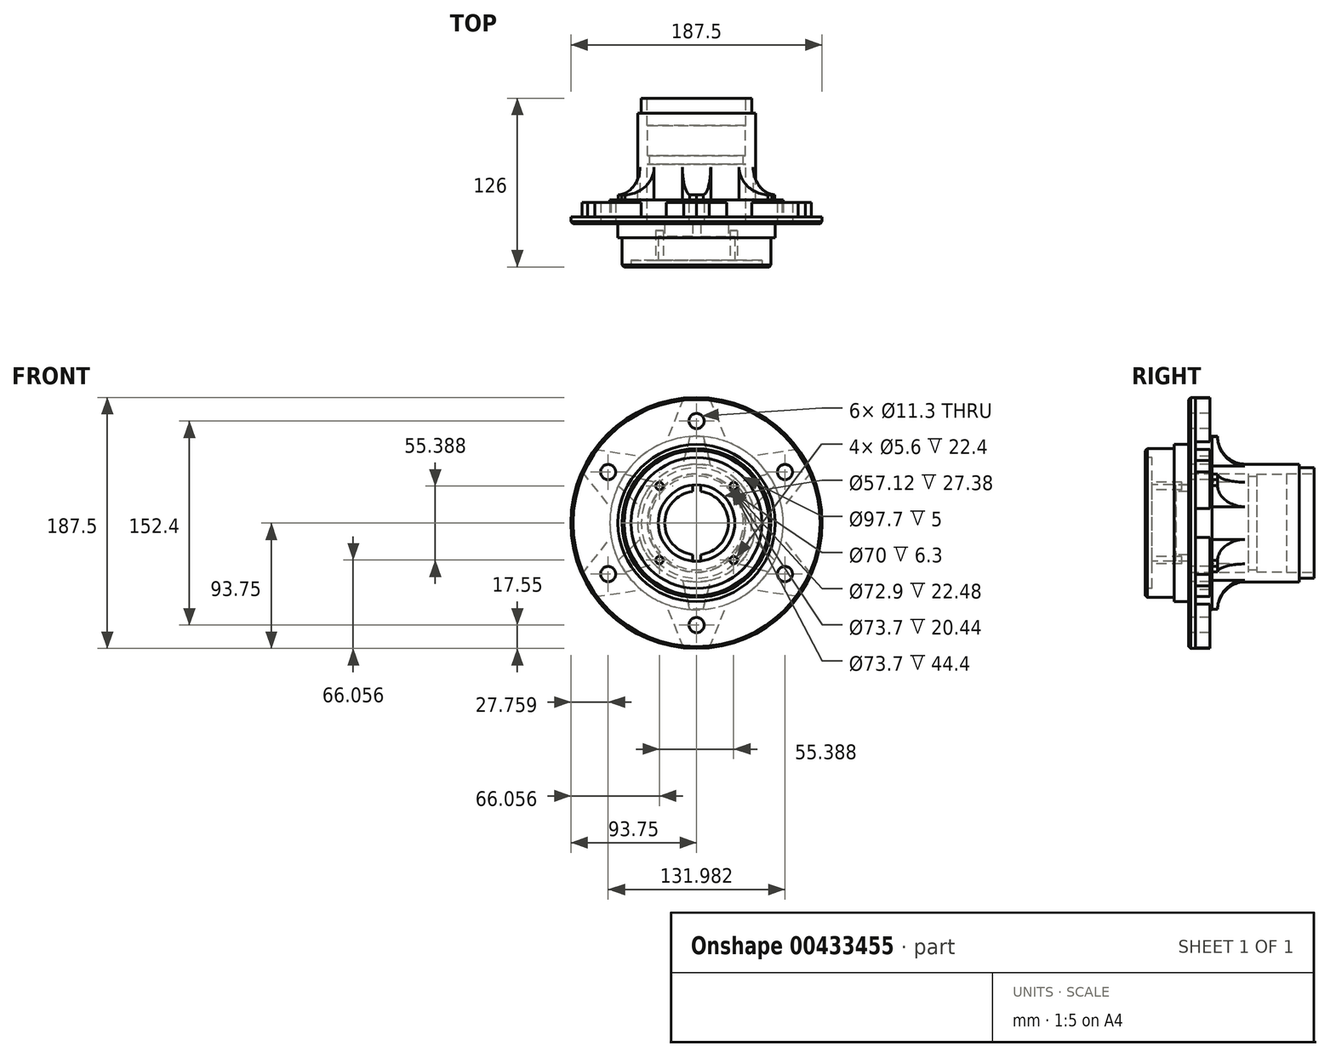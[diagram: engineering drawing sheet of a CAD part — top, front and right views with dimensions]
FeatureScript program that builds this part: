
annotation { "Feature Type Name" : "Feature", "Feature Type Description" : "" }
export const myFeature = defineFeature(function(context is Context, id is Id, definition is map)
    precondition{}
    {
        {
            var Q0;
            Q0=qCreatedBy(makeId("Front.planeOp"),FACE);
            var sketch = newSketch(context, id + "F0", { "sketchPlane" : qUnion([Q0])});
            skCircle(sketch, "E0", {"center": v(0, 0) * mm, "radius": 93.75 * mm});
            skSolve(sketch);
        }
        {
            var Q0;
            Q0=makeQuery(id+"F0.imprint","IMPRINT",FACE,{"disambiguationData":[TD([[makeQuery(id+"F0.imprint","IMPRINT",EDGE,{"derivedFrom":sQuery(id+"F0.wireOp",EDGE,"E0")}),1.0]])]});
            extrude(context, id + "F1", {"entities" : qUnion([Q0]), "endBound" : BoundingType.SYMMETRIC, "depth" : 5 * mm});
        }
        {
            var Q0;
            Q0=makeQuery(id+"F1.opExtrude","CAP_FACE",FACE,{"disambiguationData":[OSD([sQuery(id+"F0.wireOp",EDGE,"E0")])],"isStart":false});
            var sketch = newSketch(context, id + "F2", { "sketchPlane" : qUnion([Q0])});
            skCircle(sketch, "E1", {"center": v(0, 0) * mm, "radius": 58.67 * mm});
            skSolve(sketch);
        }
        {
            var Q0;
            Q0 = qSketchRegion(id + "F2", true);
            extrude(context, id + "F3", {"entities" : qUnion([Q0]), "operationType" : NewBodyOperationType.ADD, "depth" : 10.7 * mm});
        }
        {
            var Q0;
            Q0=makeQuery(id+"F3.opExtrude","CAP_FACE",FACE,{"disambiguationData":[OSD([sQuery(id+"F2.wireOp",EDGE,"E1")])],"isStart":false});
            var sketch = newSketch(context, id + "F4", { "sketchPlane" : qUnion([Q0])});
            skCircle(sketch, "E2", {"center": v(0, 0) * mm, "radius": 55.62 * mm});
            skSolve(sketch);
        }
        {
            var Q0;
            Q0 = qSketchRegion(id + "F4", true);
            extrude(context, id + "F5", {"entities" : qUnion([Q0]), "operationType" : NewBodyOperationType.ADD, "depth" : 21.7 * mm});
        }
        {
            var Q0;
            Q0=makeQuery(id+"F5.opExtrude","CAP_FACE",FACE,{"disambiguationData":[OSD([sQuery(id+"F4.wireOp",EDGE,"E2")])],"isStart":false});
            var sketch = newSketch(context, id + "F6", { "sketchPlane" : qUnion([Q0])});
            skCircle(sketch, "E3", {"center": v(0, 0) * mm, "radius": 48.85 * mm});
            skSolve(sketch);
        }
        {
            var Q0;
            Q0 = qSketchRegion(id + "F6", true);
            extrude(context, id + "F7", {"entities" : qUnion([Q0]), "operationType" : NewBodyOperationType.REMOVE, "oppositeDirection" : true, "depth" : 5 * mm});
        }
        {
            var Q0;
            Q0=makeQuery(id+"F7.boolean.opBoolean","COPY",FACE,{"derivedFrom":makeQuery(id+"F7.opExtrude","CAP_FACE",FACE,{"disambiguationData":[OSD([sQuery(id+"F6.wireOp",EDGE,"E3")])],"isStart":false})});
            var sketch = newSketch(context, id + "F8", { "sketchPlane" : qUnion([Q0])});
            skCircle(sketch, "E4", {"center": v(0, 0) * mm, "radius": 28.56 * mm});
            skSolve(sketch);
        }
        {
            var Q0;
            Q0=makeQuery(id+"F8.imprint","IMPRINT",FACE,{"disambiguationData":[TD([[makeQuery(id+"F8.imprint","IMPRINT",EDGE,{"derivedFrom":sQuery(id+"F8.wireOp",EDGE,"E4")}),1.0]])]});
            extrude(context, id + "F9", {"entities" : qUnion([Q0]), "operationType" : NewBodyOperationType.REMOVE, "oppositeDirection" : true, "depth" : 17.9 * mm});
        }
        {
            var Q0;
            Q0=makeQuery(id+"F9.boolean.opBoolean","COPY",FACE,{"derivedFrom":makeQuery(id+"F9.opExtrude","CAP_FACE",FACE,{"disambiguationData":[OSD([sQuery(id+"F8.wireOp",EDGE,"E4")])],"isStart":false})});
            var sketch = newSketch(context, id + "F10", { "sketchPlane" : qUnion([Q0])});
            skCircle(sketch, "E5", {"center": v(0, 0) * mm, "radius": 23.8 * mm});
            skSolve(sketch);
        }
        {
            var Q0;
            Q0 = qSketchRegion(id + "F10", true);
            extrude(context, id + "F11", {"entities" : qUnion([Q0]), "operationType" : NewBodyOperationType.REMOVE, "oppositeDirection" : true, "depth" : 9.3 * mm});
        }
        {
            var Q0;
            Q0=makeQuery(id+"F1.opExtrude","CAP_FACE",FACE,{"disambiguationData":[OSD([sQuery(id+"F0.wireOp",EDGE,"E0")])],"isStart":true});
            var sketch = newSketch(context, id + "F12", { "sketchPlane" : qUnion([Q0])});
            skLineSegment(sketch, "E6", {"start": v(0, -93.75) * mm, "end": v(9.62, -93.26) * mm});
            skLineSegment(sketch, "E7", {"start": v(9.62, -93.26) * mm, "end": v(22.62, -60.6) * mm});
            skLineSegment(sketch, "E8.MirrorCS", {"start": v(-9.62, -93.26) * mm, "end": v(-22.62, -60.6) * mm});
            skLineSegment(sketch, "E9", {"start": v(-9.62, -93.26) * mm, "end": v(0, -93.75) * mm});
            skLineSegment(sketch, "E10", {"start": v(22.62, -60.6) * mm, "end": v(-22.62, -60.6) * mm});
            skLineSegment(sketch, "E11.1.0", {"start": v(63.8, -10.71) * mm, "end": v(41.18, -49.89) * mm});
            skLineSegment(sketch, "E11.1.1", {"start": v(85.57, -38.3) * mm, "end": v(63.8, -10.71) * mm});
            skLineSegment(sketch, "E11.1.2", {"start": v(75.95, -54.96) * mm, "end": v(81.19, -46.88) * mm});
            skLineSegment(sketch, "E11.1.3", {"start": v(81.19, -46.88) * mm, "end": v(85.57, -38.3) * mm});
            skLineSegment(sketch, "E11.1.4", {"start": v(75.95, -54.96) * mm, "end": v(41.18, -49.89) * mm});
            skLineSegment(sketch, "E11.2.0", {"start": v(41.18, 49.89) * mm, "end": v(63.8, 10.71) * mm});
            skLineSegment(sketch, "E11.2.1", {"start": v(75.95, 54.96) * mm, "end": v(41.18, 49.89) * mm});
            skLineSegment(sketch, "E11.2.2", {"start": v(85.57, 38.3) * mm, "end": v(81.19, 46.87) * mm});
            skLineSegment(sketch, "E11.2.3", {"start": v(81.19, 46.87) * mm, "end": v(75.95, 54.96) * mm});
            skLineSegment(sketch, "E11.2.4", {"start": v(85.57, 38.3) * mm, "end": v(63.8, 10.71) * mm});
            skLineSegment(sketch, "E11.3.0", {"start": v(-22.62, 60.6) * mm, "end": v(22.62, 60.6) * mm});
            skLineSegment(sketch, "E11.3.1", {"start": v(-9.62, 93.26) * mm, "end": v(-22.62, 60.6) * mm});
            skLineSegment(sketch, "E11.3.2", {"start": v(9.62, 93.26) * mm, "end": v(0, 93.75) * mm});
            skLineSegment(sketch, "E11.3.3", {"start": v(0, 93.75) * mm, "end": v(-9.62, 93.26) * mm});
            skLineSegment(sketch, "E11.3.4", {"start": v(9.62, 93.26) * mm, "end": v(22.62, 60.6) * mm});
            skLineSegment(sketch, "E11.4.0", {"start": v(-63.8, 10.71) * mm, "end": v(-41.18, 49.89) * mm});
            skLineSegment(sketch, "E11.4.1", {"start": v(-85.57, 38.3) * mm, "end": v(-63.8, 10.71) * mm});
            skLineSegment(sketch, "E11.4.2", {"start": v(-75.95, 54.96) * mm, "end": v(-81.19, 46.88) * mm});
            skLineSegment(sketch, "E11.4.3", {"start": v(-81.19, 46.88) * mm, "end": v(-85.57, 38.3) * mm});
            skLineSegment(sketch, "E11.4.4", {"start": v(-75.95, 54.96) * mm, "end": v(-41.18, 49.89) * mm});
            skLineSegment(sketch, "E11.5.0", {"start": v(-41.18, -49.89) * mm, "end": v(-63.8, -10.71) * mm});
            skLineSegment(sketch, "E11.5.1", {"start": v(-75.95, -54.96) * mm, "end": v(-41.18, -49.89) * mm});
            skLineSegment(sketch, "E11.5.2", {"start": v(-85.57, -38.3) * mm, "end": v(-81.19, -46.88) * mm});
            skLineSegment(sketch, "E11.5.3", {"start": v(-81.19, -46.88) * mm, "end": v(-75.95, -54.96) * mm});
            skLineSegment(sketch, "E11.5.4", {"start": v(-85.57, -38.3) * mm, "end": v(-63.8, -10.71) * mm});
            skPoint(sketch, "E11.center", {"position": v(0, 0) * mm});
            skSolve(sketch);
        }
        {
            var Q0;
            Q0 = qSketchRegion(id + "F12", true);
            extrude(context, id + "F13", {"entities" : qUnion([Q0]), "operationType" : NewBodyOperationType.ADD, "depth" : 10.8 * mm});
        }
        {
            var Q0;
            {var subQ0=sQuery(id+"F0.wireOp",EDGE,"E0");var subQ1=makeQuery(id+"F1.opExtrude","CAP_FACE",FACE,{"disambiguationData":[OSD([subQ0])],"isStart":true});Q0=makeQuery(id+"F13.boolean.opBoolean","SPLIT",FACE,{"disambiguationData":[TD([makeQuery(id+"F1.opExtrude","SWEPT_FACE",FACE,{"disambiguationData":[OSD([subQ0])]}),subQ1,makeQuery(id+"F13.opExtrude","SWEPT_FACE",FACE,{"disambiguationData":[OSD([sQuery(id+"F12.wireOp",EDGE,"E6")])]}),makeQuery(id+"F13.opExtrude","SWEPT_FACE",FACE,{"disambiguationData":[OSD([sQuery(id+"F12.wireOp",EDGE,"E7")])]}),makeQuery(id+"F13.opExtrude","SWEPT_FACE",FACE,{"disambiguationData":[OSD([sQuery(id+"F12.wireOp",EDGE,"E8.MirrorCS")])]}),makeQuery(id+"F13.opExtrude","SWEPT_FACE",FACE,{"disambiguationData":[OSD([sQuery(id+"F12.wireOp",EDGE,"E9")])]}),makeQuery(id+"F13.opExtrude","SWEPT_FACE",FACE,{"disambiguationData":[OSD([sQuery(id+"F12.wireOp",EDGE,"E10")])]}),makeQuery(id+"F13.opExtrude","SWEPT_FACE",FACE,{"disambiguationData":[OSD([sQuery(id+"F12.wireOp",EDGE,"E11.1.0")])]}),makeQuery(id+"F13.opExtrude","SWEPT_FACE",FACE,{"disambiguationData":[OSD([sQuery(id+"F12.wireOp",EDGE,"E11.1.1")])]}),makeQuery(id+"F13.opExtrude","SWEPT_FACE",FACE,{"disambiguationData":[OSD([sQuery(id+"F12.wireOp",EDGE,"E11.1.2")])]}),makeQuery(id+"F13.opExtrude","SWEPT_FACE",FACE,{"disambiguationData":[OSD([sQuery(id+"F12.wireOp",EDGE,"E11.1.3")])]}),makeQuery(id+"F13.opExtrude","SWEPT_FACE",FACE,{"disambiguationData":[OSD([sQuery(id+"F12.wireOp",EDGE,"E11.1.4")])]}),makeQuery(id+"F13.opExtrude","SWEPT_FACE",FACE,{"disambiguationData":[OSD([sQuery(id+"F12.wireOp",EDGE,"E11.2.0")])]}),makeQuery(id+"F13.opExtrude","SWEPT_FACE",FACE,{"disambiguationData":[OSD([sQuery(id+"F12.wireOp",EDGE,"E11.2.1")])]}),makeQuery(id+"F13.opExtrude","SWEPT_FACE",FACE,{"disambiguationData":[OSD([sQuery(id+"F12.wireOp",EDGE,"E11.2.2")])]}),makeQuery(id+"F13.opExtrude","SWEPT_FACE",FACE,{"disambiguationData":[OSD([sQuery(id+"F12.wireOp",EDGE,"E11.2.3")])]}),makeQuery(id+"F13.opExtrude","SWEPT_FACE",FACE,{"disambiguationData":[OSD([sQuery(id+"F12.wireOp",EDGE,"E11.2.4")])]}),makeQuery(id+"F13.opExtrude","SWEPT_FACE",FACE,{"disambiguationData":[OSD([sQuery(id+"F12.wireOp",EDGE,"E11.3.0")])]}),makeQuery(id+"F13.opExtrude","SWEPT_FACE",FACE,{"disambiguationData":[OSD([sQuery(id+"F12.wireOp",EDGE,"E11.3.1")])]}),makeQuery(id+"F13.opExtrude","SWEPT_FACE",FACE,{"disambiguationData":[OSD([sQuery(id+"F12.wireOp",EDGE,"E11.3.2")])]}),makeQuery(id+"F13.opExtrude","SWEPT_FACE",FACE,{"disambiguationData":[OSD([sQuery(id+"F12.wireOp",EDGE,"E11.3.3")])]}),makeQuery(id+"F13.opExtrude","SWEPT_FACE",FACE,{"disambiguationData":[OSD([sQuery(id+"F12.wireOp",EDGE,"E11.3.4")])]}),makeQuery(id+"F13.opExtrude","SWEPT_FACE",FACE,{"disambiguationData":[OSD([sQuery(id+"F12.wireOp",EDGE,"E11.4.0")])]}),makeQuery(id+"F13.opExtrude","SWEPT_FACE",FACE,{"disambiguationData":[OSD([sQuery(id+"F12.wireOp",EDGE,"E11.4.1")])]}),makeQuery(id+"F13.opExtrude","SWEPT_FACE",FACE,{"disambiguationData":[OSD([sQuery(id+"F12.wireOp",EDGE,"E11.4.2")])]}),makeQuery(id+"F13.opExtrude","SWEPT_FACE",FACE,{"disambiguationData":[OSD([sQuery(id+"F12.wireOp",EDGE,"E11.4.3")])]}),makeQuery(id+"F13.opExtrude","SWEPT_FACE",FACE,{"disambiguationData":[OSD([sQuery(id+"F12.wireOp",EDGE,"E11.4.4")])]}),makeQuery(id+"F13.opExtrude","SWEPT_FACE",FACE,{"disambiguationData":[OSD([sQuery(id+"F12.wireOp",EDGE,"E11.5.0")])]}),makeQuery(id+"F13.opExtrude","SWEPT_FACE",FACE,{"disambiguationData":[OSD([sQuery(id+"F12.wireOp",EDGE,"E11.5.1")])]}),makeQuery(id+"F13.opExtrude","SWEPT_FACE",FACE,{"disambiguationData":[OSD([sQuery(id+"F12.wireOp",EDGE,"E11.5.2")])]}),makeQuery(id+"F13.opExtrude","SWEPT_FACE",FACE,{"disambiguationData":[OSD([sQuery(id+"F12.wireOp",EDGE,"E11.5.3")])]}),makeQuery(id+"F13.opExtrude","SWEPT_FACE",FACE,{"disambiguationData":[OSD([sQuery(id+"F12.wireOp",EDGE,"E11.5.4")])]})])],"derivedFrom":subQ1});}
            var sketch = newSketch(context, id + "F14", { "sketchPlane" : qUnion([Q0])});
            skCircle(sketch, "E12", {"center": v(0, 0) * mm, "radius": 64.7 * mm});
            skSolve(sketch);
        }
        {
            var Q0;
            Q0 = qSketchRegion(id + "F14", true);
            extrude(context, id + "F15", {"entities" : qUnion([Q0]), "operationType" : NewBodyOperationType.ADD, "depth" : 88.6 * mm});
        }
        {
            var Q0;
            Q0=makeQuery(id+"F15.opExtrude","CAP_FACE",FACE,{"disambiguationData":[OSD([sQuery(id+"F14.wireOp",EDGE,"E12")])],"isStart":false});
            var sketch = newSketch(context, id + "F16", { "sketchPlane" : qUnion([Q0])});
            skCircle(sketch, "E13", {"center": v(0, 0) * mm, "radius": 44 * mm});
            skSolve(sketch);
        }
        {
            var Q0;
            Q0=makeQuery(id+"F16.imprint","IMPRINT",FACE,{"disambiguationData":[TD([[makeQuery(id+"F16.imprint","IMPRINT",EDGE,{"derivedFrom":sQuery(id+"F16.wireOp",EDGE,"E13")}),-1.0]])]});
            extrude(context, id + "F17", {"entities" : qUnion([Q0]), "operationType" : NewBodyOperationType.REMOVE, "oppositeDirection" : true, "depth" : 76 * mm});
        }
        {
            var Q0;
            Q0=makeQuery(id+"F17.boolean.opBoolean","COPY",FACE,{"derivedFrom":makeQuery(id+"F17.opExtrude","CAP_FACE",FACE,{"disambiguationData":[OSD([sQuery(id+"F14.wireOp",EDGE,"E12"),sQuery(id+"F16.wireOp",EDGE,"E13")])],"isStart":false})});
            var sketch = newSketch(context, id + "F18", { "sketchPlane" : qUnion([Q0])});
            skLineSegment(sketch, "E14", {"start": v(-5, -64.5) * mm, "end": v(-10.58, -42.7) * mm});
            skLineSegment(sketch, "E15", {"start": v(-10.58, -42.7) * mm, "end": v(0, -44) * mm});
            skLineSegment(sketch, "E16.MirrorCS", {"start": v(5, -64.5) * mm, "end": v(10.58, -42.7) * mm});
            skLineSegment(sketch, "E17.MirrorCS", {"start": v(10.58, -42.7) * mm, "end": v(0, -44) * mm});
            skLineSegment(sketch, "E18.1.0", {"start": v(53.37, -36.58) * mm, "end": v(31.7, -30.52) * mm});
            skLineSegment(sketch, "E18.1.1", {"start": v(56.03, -32.35) * mm, "end": v(53.37, -36.58) * mm});
            skLineSegment(sketch, "E18.1.2", {"start": v(56.03, -32.35) * mm, "end": v(58.36, -27.93) * mm});
            skLineSegment(sketch, "E18.1.3", {"start": v(58.36, -27.93) * mm, "end": v(42.28, -12.2) * mm});
            skLineSegment(sketch, "E18.1.4", {"start": v(42.28, -12.2) * mm, "end": v(38.1, -22) * mm});
            skLineSegment(sketch, "E18.1.5", {"start": v(31.7, -30.52) * mm, "end": v(38.1, -22) * mm});
            skLineSegment(sketch, "E18.2.0", {"start": v(58.36, 27.93) * mm, "end": v(42.28, 12.2) * mm});
            skLineSegment(sketch, "E18.2.1", {"start": v(56.03, 32.35) * mm, "end": v(58.36, 27.93) * mm});
            skLineSegment(sketch, "E18.2.2", {"start": v(56.03, 32.35) * mm, "end": v(53.37, 36.58) * mm});
            skLineSegment(sketch, "E18.2.3", {"start": v(53.37, 36.58) * mm, "end": v(31.7, 30.52) * mm});
            skLineSegment(sketch, "E18.2.4", {"start": v(31.7, 30.52) * mm, "end": v(38.1, 22) * mm});
            skLineSegment(sketch, "E18.2.5", {"start": v(42.28, 12.2) * mm, "end": v(38.1, 22) * mm});
            skLineSegment(sketch, "E18.3.0", {"start": v(5, 64.5) * mm, "end": v(10.58, 42.7) * mm});
            skLineSegment(sketch, "E18.3.1", {"start": v(0, 64.7) * mm, "end": v(5, 64.5) * mm});
            skLineSegment(sketch, "E18.3.2", {"start": v(0, 64.7) * mm, "end": v(-5, 64.5) * mm});
            skLineSegment(sketch, "E18.3.3", {"start": v(-5, 64.5) * mm, "end": v(-10.58, 42.7) * mm});
            skLineSegment(sketch, "E18.3.4", {"start": v(-10.58, 42.7) * mm, "end": v(0, 44) * mm});
            skLineSegment(sketch, "E18.3.5", {"start": v(10.58, 42.7) * mm, "end": v(0, 44) * mm});
            skLineSegment(sketch, "E18.4.0", {"start": v(-53.37, 36.58) * mm, "end": v(-31.7, 30.52) * mm});
            skLineSegment(sketch, "E18.4.1", {"start": v(-56.03, 32.35) * mm, "end": v(-53.37, 36.58) * mm});
            skLineSegment(sketch, "E18.4.2", {"start": v(-56.03, 32.35) * mm, "end": v(-58.36, 27.93) * mm});
            skLineSegment(sketch, "E18.4.3", {"start": v(-58.36, 27.93) * mm, "end": v(-42.28, 12.2) * mm});
            skLineSegment(sketch, "E18.4.4", {"start": v(-42.28, 12.2) * mm, "end": v(-38.1, 22) * mm});
            skLineSegment(sketch, "E18.4.5", {"start": v(-31.7, 30.52) * mm, "end": v(-38.1, 22) * mm});
            skLineSegment(sketch, "E18.5.0", {"start": v(-58.36, -27.93) * mm, "end": v(-42.28, -12.2) * mm});
            skLineSegment(sketch, "E18.5.1", {"start": v(-56.03, -32.35) * mm, "end": v(-58.36, -27.93) * mm});
            skLineSegment(sketch, "E18.5.2", {"start": v(-56.03, -32.35) * mm, "end": v(-53.37, -36.58) * mm});
            skLineSegment(sketch, "E18.5.3", {"start": v(-53.37, -36.58) * mm, "end": v(-31.7, -30.52) * mm});
            skLineSegment(sketch, "E18.5.4", {"start": v(-31.7, -30.52) * mm, "end": v(-38.1, -22) * mm});
            skLineSegment(sketch, "E18.5.5", {"start": v(-42.28, -12.2) * mm, "end": v(-38.1, -22) * mm});
            skPoint(sketch, "E18.center", {"position": v(0, 0) * mm});
            skLineSegment(sketch, "E19", {"start": v(-5, -64.5) * mm, "end": v(5, -64.5) * mm});
            skSolve(sketch);
        }
        {
            var Q0;
            Q0 = qSketchRegion(id + "F18", true);
            extrude(context, id + "F19", {"entities" : qUnion([Q0]), "depth" : 4 * mm});
        }
        {
            var Q0;
            Q0=makeQuery(id+"F1.opExtrude","SWEPT_BODY",BODY,{"disambiguationData":[OSD([sQuery(id+"F0.wireOp",EDGE,"E0")])]});
            var Q1;
            Q1=makeQuery(id+"F19.opExtrude","SWEPT_BODY",BODY,{"disambiguationData":[OSD([sQuery(id+"F18.wireOp",EDGE,"E18.3.0"),sQuery(id+"F18.wireOp",EDGE,"E18.3.1"),sQuery(id+"F18.wireOp",EDGE,"E18.3.2"),sQuery(id+"F18.wireOp",EDGE,"E18.3.3"),sQuery(id+"F18.wireOp",EDGE,"E18.3.4"),sQuery(id+"F18.wireOp",EDGE,"E18.3.5")])]});
            var Q2;
            Q2=makeQuery(id+"F19.opExtrude","SWEPT_BODY",BODY,{"disambiguationData":[OSD([sQuery(id+"F18.wireOp",EDGE,"E18.2.0"),sQuery(id+"F18.wireOp",EDGE,"E18.2.1"),sQuery(id+"F18.wireOp",EDGE,"E18.2.2"),sQuery(id+"F18.wireOp",EDGE,"E18.2.3"),sQuery(id+"F18.wireOp",EDGE,"E18.2.4"),sQuery(id+"F18.wireOp",EDGE,"E18.2.5")])]});
            var Q3;
            Q3=makeQuery(id+"F19.opExtrude","SWEPT_BODY",BODY,{"disambiguationData":[OSD([sQuery(id+"F18.wireOp",EDGE,"E18.1.0"),sQuery(id+"F18.wireOp",EDGE,"E18.1.1"),sQuery(id+"F18.wireOp",EDGE,"E18.1.2"),sQuery(id+"F18.wireOp",EDGE,"E18.1.3"),sQuery(id+"F18.wireOp",EDGE,"E18.1.4"),sQuery(id+"F18.wireOp",EDGE,"E18.1.5")])]});
            var Q4;
            Q4=makeQuery(id+"F19.opExtrude","SWEPT_BODY",BODY,{"disambiguationData":[OSD([sQuery(id+"F18.wireOp",EDGE,"E14"),sQuery(id+"F18.wireOp",EDGE,"E15"),sQuery(id+"F18.wireOp",EDGE,"E16.MirrorCS"),sQuery(id+"F18.wireOp",EDGE,"E17.MirrorCS"),sQuery(id+"F18.wireOp",EDGE,"E19")])]});
            var Q5;
            Q5=makeQuery(id+"F19.opExtrude","SWEPT_BODY",BODY,{"disambiguationData":[OSD([sQuery(id+"F18.wireOp",EDGE,"E18.5.0"),sQuery(id+"F18.wireOp",EDGE,"E18.5.1"),sQuery(id+"F18.wireOp",EDGE,"E18.5.2"),sQuery(id+"F18.wireOp",EDGE,"E18.5.3"),sQuery(id+"F18.wireOp",EDGE,"E18.5.4"),sQuery(id+"F18.wireOp",EDGE,"E18.5.5")])]});
            var Q6;
            Q6=makeQuery(id+"F19.opExtrude","SWEPT_BODY",BODY,{"disambiguationData":[OSD([sQuery(id+"F18.wireOp",EDGE,"E18.4.0"),sQuery(id+"F18.wireOp",EDGE,"E18.4.1"),sQuery(id+"F18.wireOp",EDGE,"E18.4.2"),sQuery(id+"F18.wireOp",EDGE,"E18.4.3"),sQuery(id+"F18.wireOp",EDGE,"E18.4.4"),sQuery(id+"F18.wireOp",EDGE,"E18.4.5")])]});
            booleanBodies(context, id + "F20", {"operationType" : BooleanOperationType.UNION, "tools" : qUnion([Q0, Q1, Q2, Q3, Q4, Q5, Q6])});
        }
        {
            var Q0;
            Q0=makeQuery(id+"F15.opExtrude","CAP_FACE",FACE,{"disambiguationData":[OSD([sQuery(id+"F14.wireOp",EDGE,"E12")])],"isStart":false});
            var sketch = newSketch(context, id + "F21", { "sketchPlane" : qUnion([Q0])});
            skCircle(sketch, "E20", {"center": v(0, 0) * mm, "radius": 36.85 * mm});
            skSolve(sketch);
        }
        {
            var Q0;
            Q0 = qSketchRegion(id + "F21", true);
            extrude(context, id + "F22", {"entities" : qUnion([Q0]), "operationType" : NewBodyOperationType.REMOVE, "oppositeDirection" : true, "depth" : 20.44 * mm});
        }
        {
            var Q0;
            Q0=makeQuery(id+"F22.boolean.opBoolean","COPY",FACE,{"derivedFrom":makeQuery(id+"F22.opExtrude","CAP_FACE",FACE,{"disambiguationData":[OSD([sQuery(id+"F21.wireOp",EDGE,"E20")])],"isStart":false})});
            var sketch = newSketch(context, id + "F23", { "sketchPlane" : qUnion([Q0])});
            skCircle(sketch, "E21", {"center": v(0, 0) * mm, "radius": 36.45 * mm});
            skSolve(sketch);
        }
        {
            var Q0;
            Q0 = qSketchRegion(id + "F23", true);
            extrude(context, id + "F24", {"entities" : qUnion([Q0]), "operationType" : NewBodyOperationType.REMOVE, "oppositeDirection" : true, "depth" : 22.48 * mm});
        }
        {
            var Q0;
            Q0=makeQuery(id+"F24.boolean.opBoolean","COPY",FACE,{"derivedFrom":makeQuery(id+"F24.opExtrude","CAP_FACE",FACE,{"disambiguationData":[OSD([sQuery(id+"F23.wireOp",EDGE,"E21")])],"isStart":false})});
            var sketch = newSketch(context, id + "F25", { "sketchPlane" : qUnion([Q0])});
            skCircle(sketch, "E22", {"center": v(0, 0) * mm, "radius": 35 * mm});
            skSolve(sketch);
        }
        {
            var Q0;
            Q0 = qSketchRegion(id + "F25", true);
            extrude(context, id + "F26", {"entities" : qUnion([Q0]), "operationType" : NewBodyOperationType.REMOVE, "oppositeDirection" : true, "depth" : 6.3 * mm});
        }
        {
            var Q0;
            Q0=makeQuery(id+"F15.opExtrude","CAP_FACE",FACE,{"disambiguationData":[OSD([sQuery(id+"F14.wireOp",EDGE,"E12")])],"isStart":false});
            var sketch = newSketch(context, id + "F27", { "sketchPlane" : qUnion([Q0])});
            skCircle(sketch, "E23", {"center": v(0, 0) * mm, "radius": 41.25 * mm});
            skSolve(sketch);
        }
        {
            var Q0;
            Q0=makeQuery(id+"F11.boolean.opBoolean","COPY",FACE,{"derivedFrom":makeQuery(id+"F11.opExtrude","CAP_FACE",FACE,{"disambiguationData":[OSD([sQuery(id+"F10.wireOp",EDGE,"E5")])],"isStart":false})});
            extrude(context, id + "F28", {"entities" : qUnion([Q0]), "operationType" : NewBodyOperationType.REMOVE, "oppositeDirection" : true, "depth" : 44.4 * mm});
        }
        {
            var Q0;
            Q0=makeQuery(id+"F9.boolean.opBoolean","COPY",FACE,{"derivedFrom":makeQuery(id+"F9.opExtrude","CAP_FACE",FACE,{"disambiguationData":[OSD([sQuery(id+"F8.wireOp",EDGE,"E4")])],"isStart":false})});
            var sketch = newSketch(context, id + "F29", { "sketchPlane" : qUnion([Q0])});
            skArc(sketch, "E24", {"start": v(3, 29.2) * mm, "mid": v(0, 29.35) * mm, "end": v(-3, 29.2) * mm});
            skLineSegment(sketch, "E25.0", {"start": v(3, 23.8) * mm, "end": v(3, 28.56) * mm});
            skLineSegment(sketch, "E26.0", {"start": v(-3, 23.8) * mm, "end": v(-3, 28.56) * mm});
            skLineSegment(sketch, "E27", {"start": v(-3, 28.56) * mm, "end": v(-3, 29.2) * mm});
            skLineSegment(sketch, "E28", {"start": v(3, 28.56) * mm, "end": v(3, 29.2) * mm});
            skLineSegment(sketch, "E29", {"start": v(-3, 23.8) * mm, "end": v(-3, 23.67) * mm});
            skLineSegment(sketch, "E30", {"start": v(3, 23.8) * mm, "end": v(3, 23.67) * mm});
            skLineSegment(sketch, "E31.MirrorCS", {"start": v(-3, -23.8) * mm, "end": v(-3, -23.67) * mm});
            skLineSegment(sketch, "E32.MirrorCS", {"start": v(3, -23.8) * mm, "end": v(3, -23.67) * mm});
            skLineSegment(sketch, "E33.MirrorCS", {"start": v(3, -28.56) * mm, "end": v(3, -29.2) * mm});
            skLineSegment(sketch, "E34.MirrorCS", {"start": v(-3, -28.56) * mm, "end": v(-3, -29.2) * mm});
            skLineSegment(sketch, "E35.MirrorCS", {"start": v(3, -23.8) * mm, "end": v(3, -28.56) * mm});
            skLineSegment(sketch, "E36.MirrorCS", {"start": v(-3, -23.8) * mm, "end": v(-3, -28.56) * mm});
            skArc(sketch, "E37.MirrorCS", {"start": v(3, -29.2) * mm, "mid": v(0, -29.35) * mm, "end": v(-3, -29.2) * mm});
            skArc(sketch, "E38", {"start": v(-3, -23.37) * mm, "mid": v(0, -23.56) * mm, "end": v(3, -23.37) * mm});
            skLineSegment(sketch, "E39", {"start": v(-3, 23.67) * mm, "end": v(-3, 23.37) * mm});
            skLineSegment(sketch, "E40", {"start": v(3, 23.67) * mm, "end": v(3, 23.37) * mm});
            skLineSegment(sketch, "E41", {"start": v(-3, -23.67) * mm, "end": v(-3, -23.37) * mm});
            skLineSegment(sketch, "E42", {"start": v(3, -23.67) * mm, "end": v(3, -23.37) * mm});
            skArc(sketch, "E43.trimOffspring", {"start": v(3, 23.37) * mm, "mid": v(0, 23.56) * mm, "end": v(-3, 23.37) * mm});
            skSolve(sketch);
        }
        {
            var Q0;
            Q0=makeQuery(id+"F27.imprint","IMPRINT",FACE,{"disambiguationData":[TD([[makeQuery(id+"F27.imprint","IMPRINT",EDGE,{"derivedFrom":makeQuery(id+"F22.boolean.opBoolean","COPY",EDGE,{"derivedFrom":makeQuery(id+"F22.opExtrude","CAP_EDGE",EDGE,{"disambiguationData":[OSD([sQuery(id+"F21.wireOp",EDGE,"E20")])],"isStart":true})})}),1.0]])]});
            var Q1;
            Q1=makeQuery(id+"F27.imprint","IMPRINT",FACE,{"disambiguationData":[TD([[makeQuery(id+"F27.imprint","IMPRINT",EDGE,{"derivedFrom":sQuery(id+"F27.wireOp",EDGE,"E23")}),-1.0]])]});
            extrude(context, id + "F30", {"entities" : qUnion([Q0, Q1]), "operationType" : NewBodyOperationType.REMOVE, "oppositeDirection" : true, "depth" : 11.1 * mm});
        }
        {
            var Q0;
            Q0=makeQuery(id+"F20.opBoolean","INTERSECT",EDGE,{"derivedFrom":[makeQuery(id+"F17.boolean.opBoolean","COPY",FACE,{"derivedFrom":makeQuery(id+"F17.opExtrude","SWEPT_FACE",FACE,{"disambiguationData":[OSD([sQuery(id+"F16.wireOp",EDGE,"E13")])]})}),makeQuery(id+"F19.opExtrude","CAP_FACE",FACE,{"disambiguationData":[OSD([sQuery(id+"F18.wireOp",EDGE,"E14"),sQuery(id+"F18.wireOp",EDGE,"E15"),sQuery(id+"F18.wireOp",EDGE,"E16.MirrorCS"),sQuery(id+"F18.wireOp",EDGE,"E17.MirrorCS"),sQuery(id+"F18.wireOp",EDGE,"E19")])],"isStart":false})]});
            var Q1;
            Q1=makeQuery(id+"F20.opBoolean","INTERSECT",EDGE,{"derivedFrom":[makeQuery(id+"F17.boolean.opBoolean","COPY",FACE,{"derivedFrom":makeQuery(id+"F17.opExtrude","SWEPT_FACE",FACE,{"disambiguationData":[OSD([sQuery(id+"F16.wireOp",EDGE,"E13")])]})}),makeQuery(id+"F19.opExtrude","CAP_FACE",FACE,{"disambiguationData":[OSD([sQuery(id+"F18.wireOp",EDGE,"E18.5.0"),sQuery(id+"F18.wireOp",EDGE,"E18.5.1"),sQuery(id+"F18.wireOp",EDGE,"E18.5.2"),sQuery(id+"F18.wireOp",EDGE,"E18.5.3"),sQuery(id+"F18.wireOp",EDGE,"E18.5.4"),sQuery(id+"F18.wireOp",EDGE,"E18.5.5")])],"isStart":false})]});
            var Q2;
            Q2=makeQuery(id+"F20.opBoolean","INTERSECT",EDGE,{"derivedFrom":[makeQuery(id+"F17.boolean.opBoolean","COPY",FACE,{"derivedFrom":makeQuery(id+"F17.opExtrude","SWEPT_FACE",FACE,{"disambiguationData":[OSD([sQuery(id+"F16.wireOp",EDGE,"E13")])]})}),makeQuery(id+"F19.opExtrude","CAP_FACE",FACE,{"disambiguationData":[OSD([sQuery(id+"F18.wireOp",EDGE,"E18.1.0"),sQuery(id+"F18.wireOp",EDGE,"E18.1.1"),sQuery(id+"F18.wireOp",EDGE,"E18.1.2"),sQuery(id+"F18.wireOp",EDGE,"E18.1.3"),sQuery(id+"F18.wireOp",EDGE,"E18.1.4"),sQuery(id+"F18.wireOp",EDGE,"E18.1.5")])],"isStart":false})]});
            var Q3;
            Q3=makeQuery(id+"F20.opBoolean","INTERSECT",EDGE,{"derivedFrom":[makeQuery(id+"F17.boolean.opBoolean","COPY",FACE,{"derivedFrom":makeQuery(id+"F17.opExtrude","SWEPT_FACE",FACE,{"disambiguationData":[OSD([sQuery(id+"F16.wireOp",EDGE,"E13")])]})}),makeQuery(id+"F19.opExtrude","CAP_FACE",FACE,{"disambiguationData":[OSD([sQuery(id+"F18.wireOp",EDGE,"E18.4.0"),sQuery(id+"F18.wireOp",EDGE,"E18.4.1"),sQuery(id+"F18.wireOp",EDGE,"E18.4.2"),sQuery(id+"F18.wireOp",EDGE,"E18.4.3"),sQuery(id+"F18.wireOp",EDGE,"E18.4.4"),sQuery(id+"F18.wireOp",EDGE,"E18.4.5")])],"isStart":false})]});
            var Q4;
            Q4=makeQuery(id+"F20.opBoolean","INTERSECT",EDGE,{"derivedFrom":[makeQuery(id+"F17.boolean.opBoolean","COPY",FACE,{"derivedFrom":makeQuery(id+"F17.opExtrude","SWEPT_FACE",FACE,{"disambiguationData":[OSD([sQuery(id+"F16.wireOp",EDGE,"E13")])]})}),makeQuery(id+"F19.opExtrude","CAP_FACE",FACE,{"disambiguationData":[OSD([sQuery(id+"F18.wireOp",EDGE,"E18.3.0"),sQuery(id+"F18.wireOp",EDGE,"E18.3.1"),sQuery(id+"F18.wireOp",EDGE,"E18.3.2"),sQuery(id+"F18.wireOp",EDGE,"E18.3.3"),sQuery(id+"F18.wireOp",EDGE,"E18.3.4"),sQuery(id+"F18.wireOp",EDGE,"E18.3.5")])],"isStart":false})]});
            var Q5;
            Q5=makeQuery(id+"F20.opBoolean","INTERSECT",EDGE,{"derivedFrom":[makeQuery(id+"F17.boolean.opBoolean","COPY",FACE,{"derivedFrom":makeQuery(id+"F17.opExtrude","SWEPT_FACE",FACE,{"disambiguationData":[OSD([sQuery(id+"F16.wireOp",EDGE,"E13")])]})}),makeQuery(id+"F19.opExtrude","CAP_FACE",FACE,{"disambiguationData":[OSD([sQuery(id+"F18.wireOp",EDGE,"E18.2.0"),sQuery(id+"F18.wireOp",EDGE,"E18.2.1"),sQuery(id+"F18.wireOp",EDGE,"E18.2.2"),sQuery(id+"F18.wireOp",EDGE,"E18.2.3"),sQuery(id+"F18.wireOp",EDGE,"E18.2.4"),sQuery(id+"F18.wireOp",EDGE,"E18.2.5")])],"isStart":false})]});
            fillet(context, id + "F31", {"entities" : qUnion([Q0, Q1, Q2, Q3, Q4, Q5]), "radius" : 20.4 * mm, "tangentPropagation" : true, "rho" : 0.4, "crossSection" : FilletCrossSection.CONIC, "allowEdgeOverflow" : false});
        }
        {
            var Q0;
            {var subQ0=sQuery(id+"F29.wireOp",EDGE,"E29");Q0=makeQuery(id+"F29.imprint","IMPRINT",FACE,{"disambiguationData":[TD([[makeQuery(id+"F29.imprint","IMPRINT",EDGE,{"derivedFrom":subQ0}),1.0]])]});}
            var Q1;
            {var subQ10=sQuery(id+"F29.wireOp",EDGE,"E31.MirrorCS");Q1=makeQuery(id+"F29.imprint","IMPRINT",FACE,{"disambiguationData":[TD([[makeQuery(id+"F29.imprint","IMPRINT",EDGE,{"derivedFrom":subQ10}),-1.0]])]});}
            extrude(context, id + "F32", {"entities" : qUnion([Q0, Q1]), "operationType" : NewBodyOperationType.REMOVE, "oppositeDirection" : true, "depth" : 10 * mm});
        }
        {
            var Q0;
            Q0=makeQuery(id+"F26.boolean.opBoolean","COPY",FACE,{"derivedFrom":makeQuery(id+"F26.opExtrude","CAP_FACE",FACE,{"disambiguationData":[OSD([sQuery(id+"F25.wireOp",EDGE,"E22")])],"isStart":false})});
            var sketch = newSketch(context, id + "F33", { "sketchPlane" : qUnion([Q0])});
            skArc(sketch, "E44", {"start": v(-3, -33.13) * mm, "mid": v(0, -33.27) * mm, "end": v(3, -33.13) * mm});
            skArc(sketch, "E45", {"start": v(-3, -35.37) * mm, "mid": v(0, -35.5) * mm, "end": v(3, -35.37) * mm});
            skLineSegment(sketch, "E46.0", {"start": v(-3, -33.27) * mm, "end": v(-3, -35.37) * mm});
            skLineSegment(sketch, "E47.0", {"start": v(3, -33.27) * mm, "end": v(3, -35.37) * mm});
            skLineSegment(sketch, "E48", {"start": v(3, -33.27) * mm, "end": v(3, -33.13) * mm});
            skLineSegment(sketch, "E49", {"start": v(-3, -33.27) * mm, "end": v(-3, -33.13) * mm});
            skArc(sketch, "E50.MirrorCS", {"start": v(-3, 35.37) * mm, "mid": v(0, 35.5) * mm, "end": v(3, 35.37) * mm});
            skArc(sketch, "E51.MirrorCS", {"start": v(-3, 33.13) * mm, "mid": v(0, 33.27) * mm, "end": v(3, 33.13) * mm});
            skLineSegment(sketch, "E52", {"start": v(-3, 35.37) * mm, "end": v(-3, 33.13) * mm});
            skLineSegment(sketch, "E53", {"start": v(3, 35.37) * mm, "end": v(3, 33.13) * mm});
            skSolve(sketch);
        }
        {
            var Q0;
            {var subQ0=sQuery(id+"F33.wireOp",EDGE,"E51.MirrorCS");Q0=makeQuery(id+"F33.imprint","IMPRINT",FACE,{"disambiguationData":[TD([[makeQuery(id+"F33.imprint","IMPRINT",EDGE,{"derivedFrom":subQ0}),1.0]])]});}
            var Q1;
            Q1=makeQuery(id+"F33.imprint","IMPRINT",FACE,{"disambiguationData":[TD([[makeQuery(id+"F33.imprint","IMPRINT",EDGE,{"derivedFrom":sQuery(id+"F33.wireOp",EDGE,"E44")}),-1.0]])]});
            extrude(context, id + "F34", {"entities" : qUnion([Q0, Q1]), "operationType" : NewBodyOperationType.REMOVE, "oppositeDirection" : true, "depth" : 10 * mm});
        }
        {
            var Q0;
            Q0=makeQuery(id+"F1.opExtrude","CAP_FACE",FACE,{"disambiguationData":[OSD([sQuery(id+"F0.wireOp",EDGE,"E0")])],"isStart":false});
            var sketch = newSketch(context, id + "F35", { "sketchPlane" : qUnion([Q0])});
            skCircle(sketch, "E54", {"center": v(0, -76.2) * mm, "radius": 5.65 * mm});
            skCircle(sketch, "E55.1.0", {"center": v(66, -38.1) * mm, "radius": 5.65 * mm});
            skCircle(sketch, "E55.2.0", {"center": v(66, 38.1) * mm, "radius": 5.65 * mm});
            skCircle(sketch, "E55.3.0", {"center": v(0, 76.2) * mm, "radius": 5.65 * mm});
            skCircle(sketch, "E55.4.0", {"center": v(-66, 38.1) * mm, "radius": 5.65 * mm});
            skCircle(sketch, "E55.5.0", {"center": v(-66, -38.1) * mm, "radius": 5.65 * mm});
            skPoint(sketch, "E55.center", {"position": v(0, 0) * mm});
            skSolve(sketch);
        }
        {
            var Q0;
            Q0 = qSketchRegion(id + "F35", true);
            extrude(context, id + "F36", {"entities" : qUnion([Q0]), "operationType" : NewBodyOperationType.REMOVE, "oppositeDirection" : true, "depth" : 17 * mm});
        }
        {
            var Q0;
            Q0=makeQuery(id+"F7.boolean.opBoolean","COPY",FACE,{"derivedFrom":makeQuery(id+"F7.opExtrude","CAP_FACE",FACE,{"disambiguationData":[OSD([sQuery(id+"F6.wireOp",EDGE,"E3")])],"isStart":false})});
            var sketch = newSketch(context, id + "F37", { "sketchPlane" : qUnion([Q0])});
            skCircle(sketch, "E56", {"center": v(-27.7, -27.7) * mm, "radius": 2.8 * mm});
            skCircle(sketch, "E57.1.0", {"center": v(27.7, -27.7) * mm, "radius": 2.8 * mm});
            skCircle(sketch, "E57.2.0", {"center": v(27.7, 27.7) * mm, "radius": 2.8 * mm});
            skCircle(sketch, "E57.3.0", {"center": v(-27.7, 27.7) * mm, "radius": 2.8 * mm});
            skPoint(sketch, "E57.center", {"position": v(0, 0) * mm});
            skSolve(sketch);
        }
        {
            var Q0;
            Q0 = qSketchRegion(id + "F37", true);
            extrude(context, id + "F38", {"entities" : qUnion([Q0]), "operationType" : NewBodyOperationType.REMOVE, "oppositeDirection" : true, "depth" : 22.4 * mm});
        }
        {
            var Q0;
            Q0=makeQuery(id+"F1.opExtrude","CAP_EDGE",EDGE,{"disambiguationData":[OSD([sQuery(id+"F0.wireOp",EDGE,"E0")])],"isStart":false});
            var Q1;
            Q1=makeQuery(id+"F5.opExtrude","CAP_EDGE",EDGE,{"disambiguationData":[OSD([sQuery(id+"F4.wireOp",EDGE,"E2")])],"isStart":false});
            chamfer(context, id + "F39", {"entities" : qUnion([Q0, Q1]), "width" : 1.5 * mm, "tangentPropagation" : true});
        }
        {
            var Q0;
            Q0=makeQuery(id+"F26.boolean.opBoolean","COPY",FACE,{"derivedFrom":makeQuery(id+"F26.opExtrude","CAP_FACE",FACE,{"disambiguationData":[OSD([sQuery(id+"F25.wireOp",EDGE,"E22")])],"isStart":false})});
            var sketch = newSketch(context, id + "F40", { "sketchPlane" : qUnion([Q0])});
            skCircle(sketch, "E58", {"center": v(0, 0) * mm, "radius": 36.85 * mm});
            skSolve(sketch);
        }
        {
            var Q0;
            Q0 = qSketchRegion(id + "F40", true);
            extrude(context, id + "F41", {"entities" : qUnion([Q0]), "operationType" : NewBodyOperationType.REMOVE, "oppositeDirection" : true, "depth" : 44.4 * mm});
        }
    });
